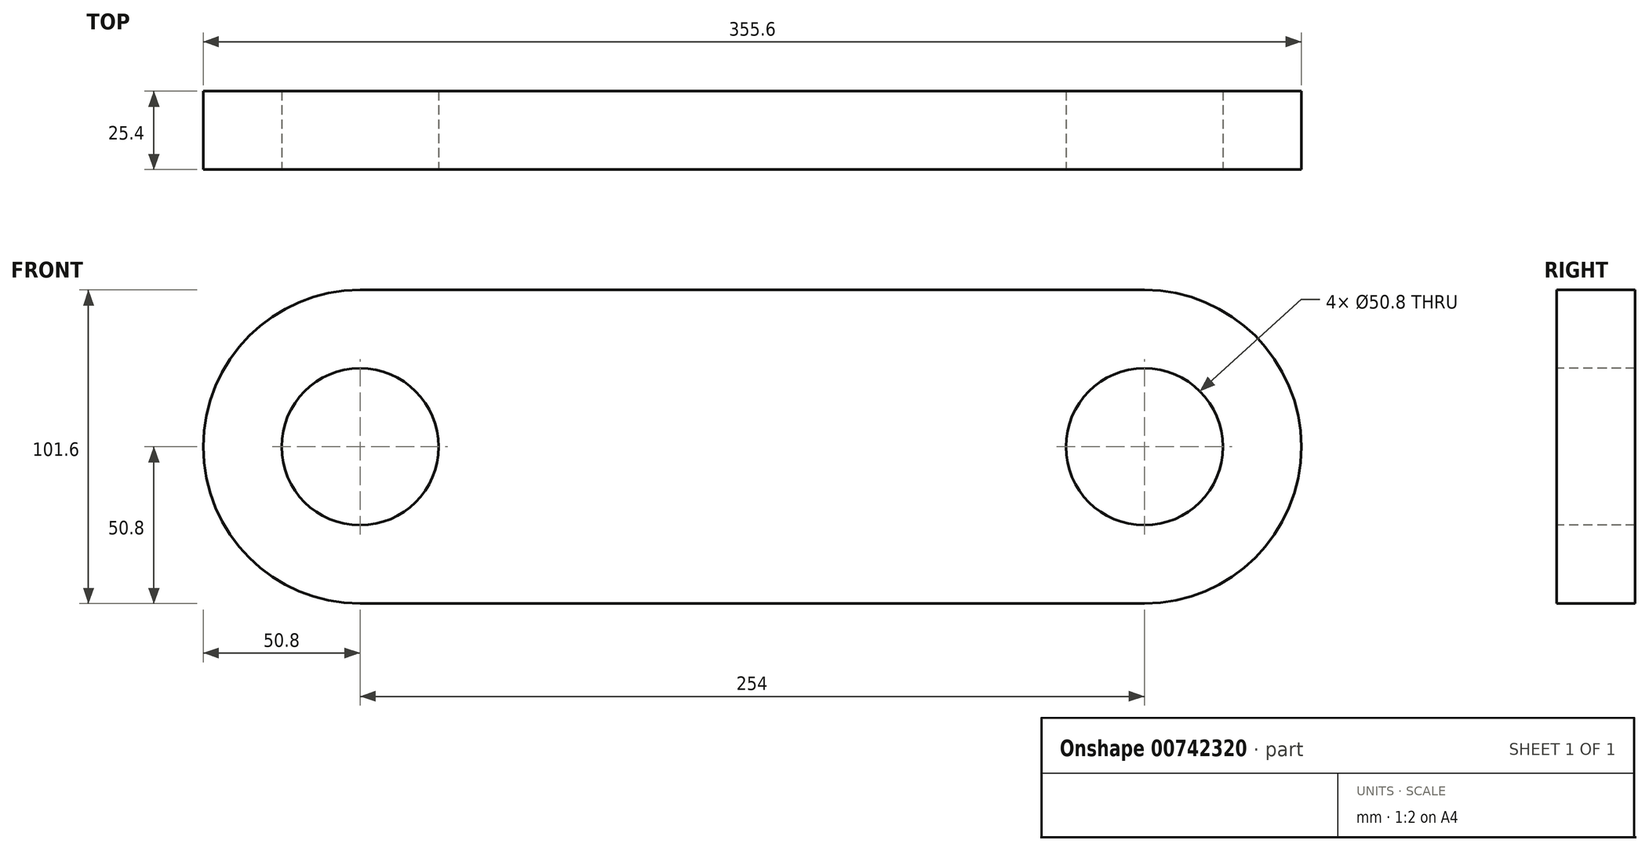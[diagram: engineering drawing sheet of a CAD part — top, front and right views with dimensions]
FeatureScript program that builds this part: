
annotation { "Feature Type Name" : "Feature", "Feature Type Description" : "" }
export const myFeature = defineFeature(function(context is Context, id is Id, definition is map)
    precondition{}
    {
        {
            var Q0;
            Q0=qCreatedBy(makeId("Front.planeOp"),FACE);
            var sketch = newSketch(context, id + "F0", { "sketchPlane" : qUnion([Q0])});
            skLineSegment(sketch, "E0.bottom", {"start": v(-127, 50.8) * mm, "end": v(127, 50.8) * mm});
            skLineSegment(sketch, "E0.top", {"start": v(-127, -50.8) * mm, "end": v(127, -50.8) * mm});
            skArc(sketch, "E1", {"start": v(-127, 50.8) * mm, "mid": v(-177.8, 0) * mm, "end": v(-127, -50.8) * mm});
            skArc(sketch, "E2", {"start": v(127, -50.8) * mm, "mid": v(177.8, 0) * mm, "end": v(127, 50.8) * mm});
            skSolve(sketch);
        }
        {
            var Q0;
            Q0=qSketchRegion(id+"F0",true);
            extrude(context, id + "F1", {"entities" : qUnion([Q0]), "endBound" : BoundingType.SYMMETRIC, "depth" : 25.4 * mm, "offsetDistance" : 25.4 * mm});
        }
        {
            var Q0;
            Q0=makeQuery(id+"F1.opExtrude","CAP_FACE",FACE,{"disambiguationData":[OSD([sQuery(id+"F0.wireOp",EDGE,"E0.bottom"),sQuery(id+"F0.wireOp",EDGE,"E0.top"),sQuery(id+"F0.wireOp",EDGE,"E1"),sQuery(id+"F0.wireOp",EDGE,"E2")])],"isStart":false});
            var sketch = newSketch(context, id + "F2", { "sketchPlane" : qUnion([Q0])});
            skCircle(sketch, "E3", {"center": v(-127, 0) * mm, "radius": 25.4 * mm});
            skCircle(sketch, "E4", {"center": v(127, 0) * mm, "radius": 25.4 * mm});
            skSolve(sketch);
        }
        {
            var Q0;
            Q0=qSketchRegion(id+"F2",true);
            extrude(context, id + "F3", {"entities" : qUnion([Q0]), "operationType" : NewBodyOperationType.REMOVE, "endBound" : BoundingType.THROUGH_ALL, "oppositeDirection" : true, "depth" : 25.4 * mm, "offsetDistance" : 25.4 * mm});
        }
    });
